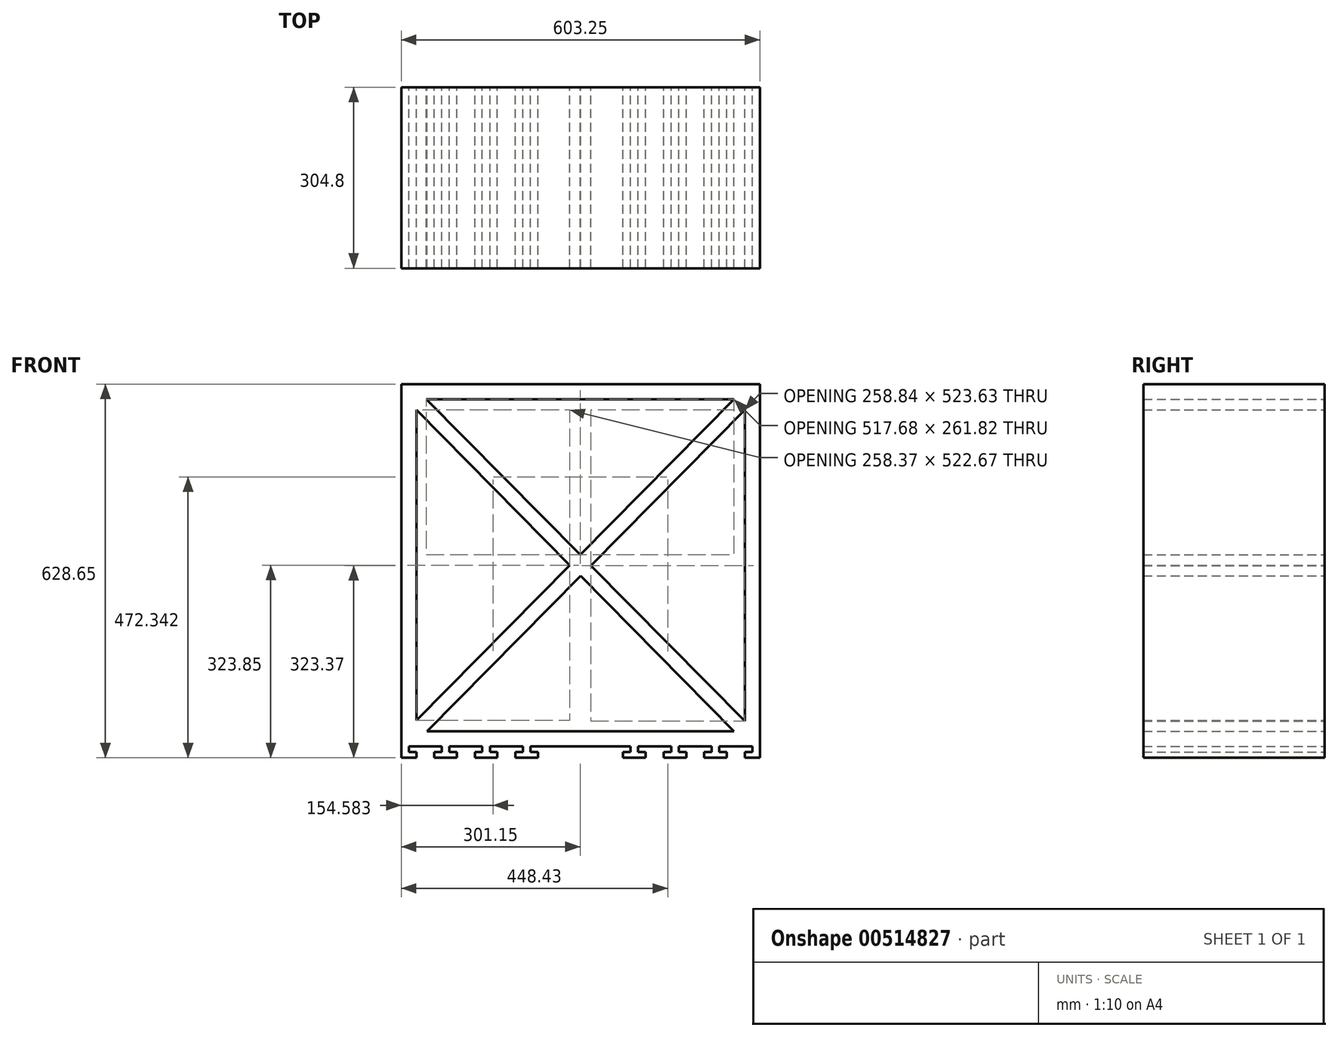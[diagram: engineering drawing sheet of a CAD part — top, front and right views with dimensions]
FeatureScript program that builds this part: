
annotation { "Feature Type Name" : "Feature", "Feature Type Description" : "" }
export const myFeature = defineFeature(function(context is Context, id is Id, definition is map)
    precondition{}
    {
        {
            var Q0;
            Q0=qCreatedBy(makeId("Front.planeOp"),FACE);
            var sketch = newSketch(context, id + "F0", { "sketchPlane" : qUnion([Q0])});
            skLineSegment(sketch, "E0.bottom", {"start": v(0, 0) * mm, "end": v(603.25, 0) * mm});
            skLineSegment(sketch, "E0.top", {"start": v(0, 609.6) * mm, "end": v(603.25, 609.6) * mm});
            skLineSegment(sketch, "E0.left", {"start": v(0, 0) * mm, "end": v(0, 609.6) * mm});
            skLineSegment(sketch, "E0.right", {"start": v(603.25, 0) * mm, "end": v(603.25, 609.6) * mm});
            skLineSegment(sketch, "E1.0", {"start": v(577.85, 42.5) * mm, "end": v(577.85, 566.14) * mm});
            skLineSegment(sketch, "E1.1", {"start": v(43.26, 25.4) * mm, "end": v(560, 25.4) * mm});
            skLineSegment(sketch, "E1.2", {"start": v(25.4, 43.46) * mm, "end": v(25.4, 566.14) * mm});
            skLineSegment(sketch, "E1.3", {"start": v(42.3, 584.2) * mm, "end": v(560, 584.2) * mm});
            skLineSegment(sketch, "E2.0", {"start": v(43.26, 25.4) * mm, "end": v(301.63, 286.74) * mm});
            skLineSegment(sketch, "E3.0", {"start": v(25.4, 43.46) * mm, "end": v(283.77, 304.8) * mm});
            skLineSegment(sketch, "E4.0", {"start": v(25.4, 566.14) * mm, "end": v(283.77, 304.8) * mm});
            skLineSegment(sketch, "E5.0", {"start": v(42.3, 584.2) * mm, "end": v(301.15, 322.38) * mm});
            skLineSegment(sketch, "E6.trimOffspring", {"start": v(319, 304.32) * mm, "end": v(577.85, 42.5) * mm});
            skLineSegment(sketch, "E7.trimOffspring", {"start": v(301.63, 286.74) * mm, "end": v(560, 25.4) * mm});
            skLineSegment(sketch, "E8.trimOffspring", {"start": v(319, 304.32) * mm, "end": v(577.85, 566.14) * mm});
            skLineSegment(sketch, "E9.trimOffspring", {"start": v(301.15, 322.38) * mm, "end": v(560, 584.2) * mm});
            skSolve(sketch);
        }
        {
            var Q0;
            Q0=makeQuery(id+"F0.imprint","IMPRINT",FACE,{"disambiguationData":[TD([[makeQuery(id+"F0.imprint","IMPRINT",EDGE,{"derivedFrom":sQuery(id+"F0.wireOp",EDGE,"E0.bottom")}),1.0]])]});
            extrude(context, id + "F1", {"entities" : qUnion([Q0]), "depth" : 304.8 * mm, "offsetDistance" : 25.4 * mm});
        }
        {
            var Q0;
            Q0=qCreatedBy(makeId("Front.planeOp"),FACE);
            var sketch = newSketch(context, id + "F2", { "sketchPlane" : qUnion([Q0])});
            skLineSegment(sketch, "E10", {"start": v(0, 0) * mm, "end": v(0, -19.05) * mm});
            skLineSegment(sketch, "E11", {"start": v(0, -19.05) * mm, "end": v(25.4, -19.05) * mm});
            skLineSegment(sketch, "E12", {"start": v(25.4, -19.05) * mm, "end": v(25.4, -9.52) * mm});
            skLineSegment(sketch, "E13", {"start": v(25.4, -9.52) * mm, "end": v(12.7, -9.53) * mm});
            skLineSegment(sketch, "E14", {"start": v(12.7, -9.52) * mm, "end": v(12.7, 0) * mm});
            skLineSegment(sketch, "E15", {"start": v(12.7, 0) * mm, "end": v(0, 0) * mm});
            skLineSegment(sketch, "E16", {"start": v(68.26, 0) * mm, "end": v(68.26, -9.53) * mm});
            skLineSegment(sketch, "E17", {"start": v(68.26, -9.53) * mm, "end": v(55.56, -9.53) * mm});
            skLineSegment(sketch, "E18", {"start": v(55.56, -9.53) * mm, "end": v(55.56, -19.05) * mm});
            skLineSegment(sketch, "E19", {"start": v(55.56, -19.05) * mm, "end": v(93.66, -19.05) * mm});
            skLineSegment(sketch, "E20", {"start": v(93.66, -19.05) * mm, "end": v(93.66, -9.53) * mm});
            skLineSegment(sketch, "E21", {"start": v(93.66, -9.53) * mm, "end": v(80.96, -9.53) * mm});
            skLineSegment(sketch, "E22", {"start": v(80.96, -9.53) * mm, "end": v(80.96, 0) * mm});
            skLineSegment(sketch, "E23", {"start": v(80.96, 0) * mm, "end": v(68.26, 0) * mm});
            skLineSegment(sketch, "E24", {"start": v(136.53, 0) * mm, "end": v(136.53, -9.52) * mm});
            skLineSegment(sketch, "E25", {"start": v(136.53, -9.53) * mm, "end": v(123.83, -9.53) * mm});
            skLineSegment(sketch, "E26", {"start": v(123.83, -9.52) * mm, "end": v(123.83, -19.05) * mm});
            skLineSegment(sketch, "E27", {"start": v(123.83, -19.05) * mm, "end": v(161.93, -19.05) * mm});
            skLineSegment(sketch, "E28", {"start": v(161.93, -19.05) * mm, "end": v(161.93, -9.53) * mm});
            skLineSegment(sketch, "E29", {"start": v(161.93, -9.53) * mm, "end": v(149.23, -9.53) * mm});
            skLineSegment(sketch, "E30", {"start": v(149.23, -9.53) * mm, "end": v(149.23, 0) * mm});
            skLineSegment(sketch, "E31", {"start": v(149.23, 0) * mm, "end": v(136.53, 0) * mm});
            skLineSegment(sketch, "E32", {"start": v(0, 0) * mm, "end": v(603.25, 0) * mm, "construction": true});
            skLineSegment(sketch, "E33", {"start": v(301.63, 0) * mm, "end": v(301.63, 169.62) * mm, "construction": true});
            skLineSegment(sketch, "E34.MirrorCS", {"start": v(534.99, -9.53) * mm, "end": v(547.69, -9.53) * mm});
            skLineSegment(sketch, "E35.MirrorCS", {"start": v(547.69, -9.53) * mm, "end": v(547.69, -19.05) * mm});
            skLineSegment(sketch, "E36.MirrorCS", {"start": v(534.99, 0) * mm, "end": v(534.99, -9.53) * mm});
            skLineSegment(sketch, "E37.MirrorCS", {"start": v(590.55, 0) * mm, "end": v(603.25, 0) * mm});
            skLineSegment(sketch, "E38.MirrorCS", {"start": v(590.55, -9.52) * mm, "end": v(590.55, 0) * mm});
            skLineSegment(sketch, "E39.MirrorCS", {"start": v(577.85, -9.52) * mm, "end": v(590.55, -9.53) * mm});
            skLineSegment(sketch, "E40.MirrorCS", {"start": v(577.85, -19.05) * mm, "end": v(577.85, -9.52) * mm});
            skLineSegment(sketch, "E41.MirrorCS", {"start": v(466.73, -9.53) * mm, "end": v(479.43, -9.53) * mm});
            skLineSegment(sketch, "E42.MirrorCS", {"start": v(466.73, 0) * mm, "end": v(466.73, -9.52) * mm});
            skLineSegment(sketch, "E43.MirrorCS", {"start": v(522.29, 0) * mm, "end": v(534.99, 0) * mm});
            skLineSegment(sketch, "E44.MirrorCS", {"start": v(509.59, -19.05) * mm, "end": v(509.59, -9.53) * mm});
            skLineSegment(sketch, "E45.MirrorCS", {"start": v(509.59, -9.53) * mm, "end": v(522.29, -9.53) * mm});
            skLineSegment(sketch, "E46.MirrorCS", {"start": v(522.29, -9.53) * mm, "end": v(522.29, 0) * mm});
            skLineSegment(sketch, "E47.MirrorCS", {"start": v(441.33, -9.53) * mm, "end": v(454.03, -9.53) * mm});
            skLineSegment(sketch, "E48.MirrorCS", {"start": v(454.03, -9.53) * mm, "end": v(454.03, 0) * mm});
            skLineSegment(sketch, "E49.MirrorCS", {"start": v(454.03, 0) * mm, "end": v(466.73, 0) * mm});
            skLineSegment(sketch, "E50.MirrorCS", {"start": v(479.43, -9.52) * mm, "end": v(479.43, -19.05) * mm});
            skLineSegment(sketch, "E51.MirrorCS", {"start": v(441.33, -19.05) * mm, "end": v(441.33, -9.53) * mm});
            skLineSegment(sketch, "E52.MirrorCS", {"start": v(603.25, -19.05) * mm, "end": v(577.85, -19.05) * mm});
            skLineSegment(sketch, "E53.MirrorCS", {"start": v(603.25, 0) * mm, "end": v(603.25, -19.05) * mm});
            skLineSegment(sketch, "E54.MirrorCS", {"start": v(547.69, -19.05) * mm, "end": v(509.59, -19.05) * mm});
            skLineSegment(sketch, "E55.MirrorCS", {"start": v(479.43, -19.05) * mm, "end": v(441.33, -19.05) * mm});
            skLineSegment(sketch, "E56", {"start": v(204.79, 0) * mm, "end": v(204.79, -9.53) * mm});
            skLineSegment(sketch, "E57", {"start": v(204.79, -9.53) * mm, "end": v(192.09, -9.53) * mm});
            skLineSegment(sketch, "E58", {"start": v(192.09, -9.53) * mm, "end": v(192.09, -19.05) * mm});
            skLineSegment(sketch, "E59", {"start": v(192.09, -19.05) * mm, "end": v(230.19, -19.05) * mm});
            skLineSegment(sketch, "E60", {"start": v(230.19, -19.05) * mm, "end": v(230.19, -9.53) * mm});
            skLineSegment(sketch, "E61", {"start": v(230.19, -9.53) * mm, "end": v(217.49, -9.53) * mm});
            skLineSegment(sketch, "E62", {"start": v(217.49, -9.53) * mm, "end": v(217.49, 0) * mm});
            skLineSegment(sketch, "E63", {"start": v(217.49, 0) * mm, "end": v(204.79, 0) * mm});
            skLineSegment(sketch, "E64.MirrorCS", {"start": v(411.16, -9.53) * mm, "end": v(411.16, -19.05) * mm});
            skLineSegment(sketch, "E65.MirrorCS", {"start": v(385.76, -9.53) * mm, "end": v(385.76, 0) * mm});
            skLineSegment(sketch, "E66.MirrorCS", {"start": v(398.46, 0) * mm, "end": v(398.46, -9.53) * mm});
            skLineSegment(sketch, "E67.MirrorCS", {"start": v(373.06, -19.05) * mm, "end": v(373.06, -9.53) * mm});
            skLineSegment(sketch, "E68.MirrorCS", {"start": v(398.46, -9.53) * mm, "end": v(411.16, -9.53) * mm});
            skLineSegment(sketch, "E69.MirrorCS", {"start": v(373.06, -9.53) * mm, "end": v(385.76, -9.53) * mm});
            skLineSegment(sketch, "E70.MirrorCS", {"start": v(385.76, 0) * mm, "end": v(398.46, 0) * mm});
            skLineSegment(sketch, "E71.MirrorCS", {"start": v(411.16, -19.05) * mm, "end": v(373.06, -19.05) * mm});
            skSolve(sketch);
        }
        {
            var Q0;
            Q0=makeQuery(id+"F2.imprint","IMPRINT",FACE,{"disambiguationData":[TD([[makeQuery(id+"F2.imprint","IMPRINT",EDGE,{"derivedFrom":sQuery(id+"F2.wireOp",EDGE,"E10")}),1.0]])]});
            var Q1;
            Q1=makeQuery(id+"F2.imprint","IMPRINT",FACE,{"disambiguationData":[TD([[makeQuery(id+"F2.imprint","IMPRINT",EDGE,{"derivedFrom":sQuery(id+"F2.wireOp",EDGE,"E16")}),1.0]])]});
            var Q2;
            Q2=makeQuery(id+"F2.imprint","IMPRINT",FACE,{"disambiguationData":[TD([[makeQuery(id+"F2.imprint","IMPRINT",EDGE,{"derivedFrom":sQuery(id+"F2.wireOp",EDGE,"E24")}),1.0]])]});
            var Q3;
            Q3=makeQuery(id+"F2.imprint","IMPRINT",FACE,{"disambiguationData":[TD([[makeQuery(id+"F2.imprint","IMPRINT",EDGE,{"derivedFrom":sQuery(id+"F2.wireOp",EDGE,"E56")}),1.0]])]});
            var Q4;
            Q4=makeQuery(id+"F2.imprint","IMPRINT",FACE,{"disambiguationData":[TD([[makeQuery(id+"F2.imprint","IMPRINT",EDGE,{"derivedFrom":sQuery(id+"F2.wireOp",EDGE,"E64.MirrorCS")}),-1.0]])]});
            var Q5;
            Q5=makeQuery(id+"F2.imprint","IMPRINT",FACE,{"disambiguationData":[TD([[makeQuery(id+"F2.imprint","IMPRINT",EDGE,{"derivedFrom":sQuery(id+"F2.wireOp",EDGE,"E41.MirrorCS")}),-1.0]])]});
            var Q6;
            Q6=makeQuery(id+"F2.imprint","IMPRINT",FACE,{"disambiguationData":[TD([[makeQuery(id+"F2.imprint","IMPRINT",EDGE,{"derivedFrom":sQuery(id+"F2.wireOp",EDGE,"E34.MirrorCS")}),-1.0]])]});
            var Q7;
            Q7=makeQuery(id+"F2.imprint","IMPRINT",FACE,{"disambiguationData":[TD([[makeQuery(id+"F2.imprint","IMPRINT",EDGE,{"derivedFrom":sQuery(id+"F2.wireOp",EDGE,"E37.MirrorCS")}),-1.0]])]});
            extrude(context, id + "F3", {"entities" : qUnion([Q0, Q1, Q2, Q3, Q4, Q5, Q6, Q7]), "operationType" : NewBodyOperationType.ADD, "depth" : 304.8 * mm, "offsetDistance" : 25.4 * mm});
        }
    });
